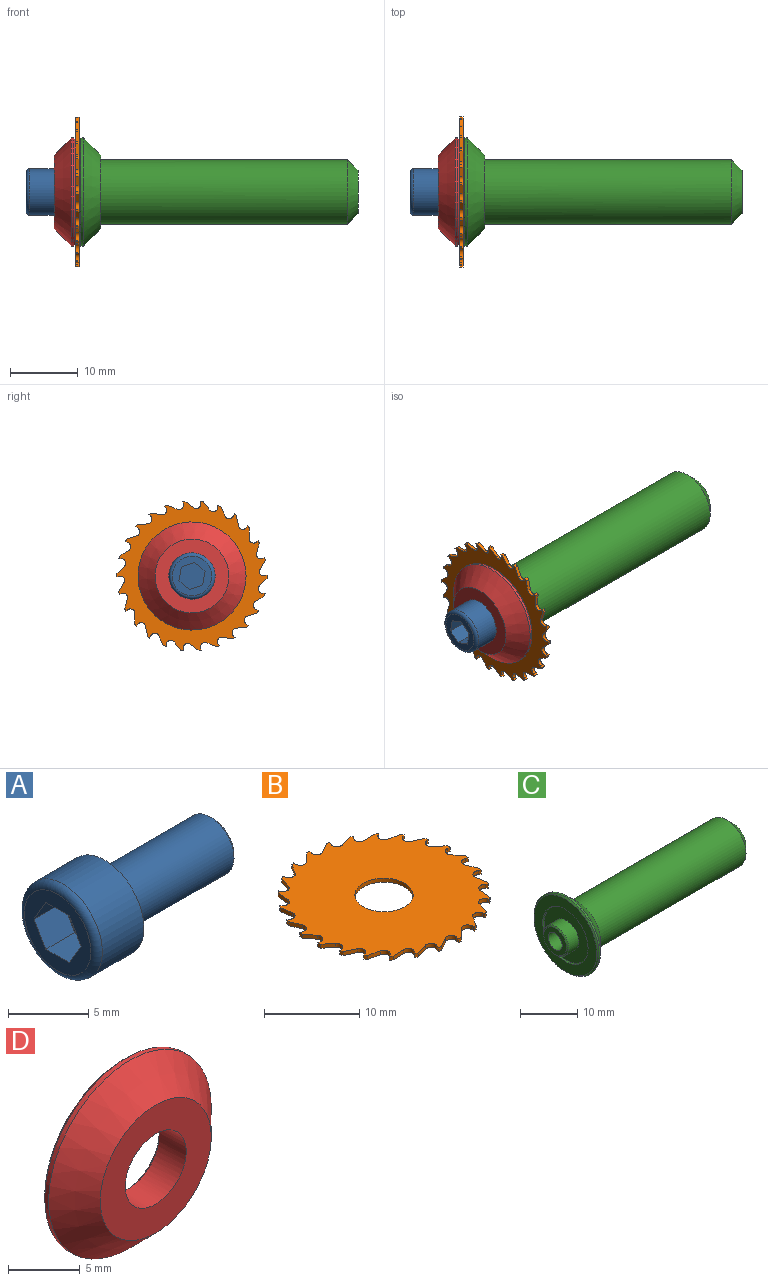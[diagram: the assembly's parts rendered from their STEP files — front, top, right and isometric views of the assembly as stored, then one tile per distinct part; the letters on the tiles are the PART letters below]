
ASSEMBLY  parts=4 mates=6
PART A: 14 faces, bbox 13.7x7.4x7.4 mm
  f0: plane 6.86x6.86mm, normal (1,0,0), area 23.3mm2, adj f1,f5
  f1: cylinder r=3.43mm len=6.86mm, axis (1,0,0), area 78.8mm2, adj f0,f2
  f2: torus R=2.92mm, axis (1,0,0), area 16.3mm2, adj f1,f3
  f3: plane 5.84x5.84mm, normal (-1,0,0), area 15.8mm2, adj f2,f6,f7,f8,f9,f10,f11
  f4: plane 3.66x3.66mm, normal (1,0,0), area 10.5mm2, adj f13
  f5: cylinder r=2.08mm len=9.27mm, axis (1,0,0), area 121.3mm2, adj f0,f13
  f6: plane 2.54x2.06mm, normal (0,0,1), area 5.2mm2, adj f3,f7,f11,f12
  f7: plane 2.54x1.79mm, normal (0,0.87,0.5), area 5.2mm2, adj f3,f6,f8,f12
  f8: plane 2.54x1.79mm, normal (0,0.87,-0.5), area 5.2mm2, adj f3,f7,f9,f12
  f9: plane 2.54x2.06mm, normal (0,0,-1), area 5.2mm2, adj f3,f8,f10,f12
  f10: plane 2.54x1.79mm, normal (0,-0.87,-0.5), area 5.2mm2, adj f3,f9,f11,f12
  f11: plane 2.54x1.79mm, normal (0,-0.87,0.5), area 5.2mm2, adj f3,f6,f10,f12
  f12: plane 4.12x3.57mm, normal (-1,0,0), area 11mm2, adj f6,f7,f8,f9,f10,f11
  f13: cone r=1.83mm half-angle=45deg, axis (-1,0,0), area 4.4mm2, adj f4,f5
PART B: 107 faces, bbox 22.1x22.2x0.5 mm
  f0: cylinder r=11.11mm len=0.51mm, axis (0,0,-1), area 0.2mm2, adj f9,f55,f70,f85
  f1: plane 0.51x0.27mm, normal (0.88,-0.48,0), area 0.2mm2, adj f8,f55,f85,f92
  f2: plane 1.45x0.62mm, normal (-0.92,-0.39,0), area 0.8mm2, adj f47,f55,f85,f106
  f3: cylinder r=11.11mm len=0.51mm, axis (0,0,-1), area 0.2mm2, adj f4,f41,f55,f85
  f4: plane 0.51x0.27mm, normal (-0.89,-0.45,0), area 0.2mm2, adj f3,f55,f85,f87
  f5: cylinder r=0.67mm len=1.23mm, axis (0,0,-1), area 0.8mm2, adj f55,f73,f77,f85
  f6: plane 0.51x0.3mm, normal (-1,0.02,0), area 0.2mm2, adj f55,f67,f85,f86
  f7: cylinder r=0.67mm len=1.12mm, axis (0,0,-1), area 0.8mm2, adj f55,f61,f85,f102
  f8: cylinder r=0.67mm len=0.99mm, axis (0,0,-1), area 0.8mm2, adj f1,f54,f55,f85
  f9: plane 1.22x1mm, normal (-0.63,-0.77,0), area 0.8mm2, adj f0,f10,f55,f85
  f10: cylinder r=0.67mm len=1.18mm, axis (0,0,-1), area 0.8mm2, adj f9,f55,f85,f95
  f11: plane 1.57x0.51mm, normal (-0.04,1,0), area 0.8mm2, adj f29,f55,f76,f85
  f12: cylinder r=11.11mm len=0.51mm, axis (0,0,-1), area 0.2mm2, adj f26,f50,f55,f85
  f13: cylinder r=11.11mm len=0.51mm, axis (0,0,-1), area 0.2mm2, adj f14,f55,f85,f102
  f14: plane 0.51x0.25mm, normal (-0.55,0.83,0), area 0.2mm2, adj f13,f22,f55,f85
  f15: cylinder r=0.67mm len=1.07mm, axis (0,0,-1), area 0.8mm2, adj f55,f85,f89,f98
  f16: plane 0.51x0.28mm, normal (0.37,0.93,0), area 0.2mm2, adj f55,f85,f91,f106
  f17: cylinder r=0.67mm len=1.21mm, axis (0,0,-1), area 0.8mm2, adj f28,f32,f55,f85
  f18: plane 1.49x0.51mm, normal (0.95,-0.32,0), area 0.8mm2, adj f48,f55,f85,f87
  f19: cylinder r=0.67mm len=1mm, axis (0,0,-1), area 0.8mm2, adj f27,f45,f55,f85
  f20: cylinder r=0.67mm len=1.06mm, axis (0,0,-1), area 0.8mm2, adj f55,f79,f85,f100
  f21: cylinder r=0.67mm len=0.93mm, axis (0,0,-1), area 0.8mm2, adj f55,f71,f74,f85
  f22: cylinder r=0.67mm len=1.21mm, axis (0,0,-1), area 0.8mm2, adj f14,f50,f55,f85
  f23: cylinder r=11.11mm len=0.51mm, axis (0,0,-1), area 0.2mm2, adj f55,f77,f83,f85
  f24: plane 0.51x0.27mm, normal (-0.88,0.48,0), area 0.2mm2, adj f30,f55,f65,f85
  f25: plane 1.42x0.68mm, normal (0.43,0.9,0), area 0.8mm2, adj f53,f55,f81,f85
  f26: plane 0.51x0.29mm, normal (-0.34,0.94,0), area 0.2mm2, adj f12,f55,f72,f85
  f27: plane 0.51x0.29mm, normal (-0.97,0.26,0), area 0.2mm2, adj f19,f36,f55,f85
  f28: plane 1.33x0.84mm, normal (-0.85,0.53,0), area 0.8mm2, adj f17,f37,f55,f85
  f29: cylinder r=11.11mm len=0.51mm, axis (0,0,-1), area 0.2mm2, adj f11,f55,f75,f85
  f30: cylinder r=11.11mm len=0.51mm, axis (0,0,-1), area 0.2mm2, adj f24,f45,f55,f85
  f31: plane 0.51x0.29mm, normal (0.97,-0.26,0), area 0.2mm2, adj f55,f85,f90,f96
  f32: plane 0.51x0.3mm, normal (0.98,0.22,0), area 0.2mm2, adj f17,f34,f55,f85
  f33: plane 0.51x0.3mm, normal (0.1,-0.99,0), area 0.2mm2, adj f46,f53,f55,f85
  f34: cylinder r=11.11mm len=0.51mm, axis (0,0,-1), area 0.2mm2, adj f32,f55,f73,f85
  f35: plane 1.26x0.95mm, normal (-0.8,-0.6,0), area 0.8mm2, adj f55,f62,f85,f91
  f36: cylinder r=11.11mm len=0.51mm, axis (0,0,-1), area 0.2mm2, adj f27,f52,f55,f85
  f37: cylinder r=11.11mm len=0.51mm, axis (0,0,-1), area 0.2mm2, adj f28,f55,f56,f85
  f38: plane 1.36x0.79mm, normal (-0.5,0.87,0), area 0.8mm2, adj f55,f85,f90,f92
  f39: cylinder r=11.11mm len=0.51mm, axis (0,0,-1), area 0.2mm2, adj f55,f61,f64,f85
  f40: plane 0.51x0.23mm, normal (-0.76,-0.65,0), area 0.2mm2, adj f55,f63,f85,f88
  f41: plane 1.57x0.51mm, normal (1,-0.08,0), area 0.8mm2, adj f3,f55,f85,f88
  f42: cylinder r=11.11mm len=0.51mm, axis (0,0,-1), area 0.2mm2, adj f54,f55,f58,f85
  f43: cylinder r=0.67mm len=1.13mm, axis (0,0,-1), area 0.8mm2, adj f49,f55,f56,f85
  f44: plane 1.42x0.68mm, normal (-0.43,-0.9,0), area 0.8mm2, adj f55,f72,f85,f103
  f45: plane 1.36x0.79mm, normal (0.5,-0.87,0), area 0.8mm2, adj f19,f30,f55,f85
  f46: cylinder r=0.67mm len=1.18mm, axis (0,0,-1), area 0.8mm2, adj f33,f55,f78,f85
  f47: cylinder r=11.11mm len=0.51mm, axis (0,0,-1), area 0.2mm2, adj f2,f55,f68,f85
  f48: cylinder r=11.11mm len=0.51mm, axis (0,0,-1), area 0.2mm2, adj f18,f55,f59,f85
  f49: plane 1.14x1.09mm, normal (-0.69,0.72,0), area 0.8mm2, adj f43,f55,f85,f96
  f50: plane 1.54x0.51mm, normal (-0.2,-0.98,0), area 0.8mm2, adj f12,f22,f55,f85
  f51: cylinder r=11.11mm len=0.51mm, axis (0,0,-1), area 0.2mm2, adj f55,f71,f79,f85
  f52: plane 1.14x1.09mm, normal (0.69,-0.72,0), area 0.8mm2, adj f36,f55,f85,f86
  f53: cylinder r=11.11mm len=0.51mm, axis (0,0,-1), area 0.2mm2, adj f25,f33,f55,f85
  f54: plane 1.51x0.51mm, normal (-0.28,0.96,0), area 0.8mm2, adj f8,f42,f55,f85
  f55: plane 22.21x22.12mm, normal (0,0,1), area 314.4mm2, adj f0,f1,f2,f3,f4,f5,f6,f7
  f56: plane 0.51x0.3mm, normal (1,-0.02,0), area 0.2mm2, adj f37,f43,f55,f85
  f57: cylinder r=0.67mm len=1.21mm, axis (0,0,-1), area 0.8mm2, adj f55,f59,f85,f104
  f58: plane 0.51x0.22mm, normal (0.74,-0.68,0), area 0.2mm2, adj f42,f55,f76,f85
  f59: plane 0.51x0.3mm, normal (-0.98,-0.22,0), area 0.2mm2, adj f48,f55,f57,f85
  f60: cylinder r=0.67mm len=1.17mm, axis (0,0,-1), area 0.8mm2, adj f55,f83,f85,f99
  f61: plane 0.51x0.22mm, normal (-0.74,0.68,0), area 0.2mm2, adj f7,f39,f55,f85
  f62: cylinder r=0.67mm len=1.07mm, axis (0,0,-1), area 0.8mm2, adj f35,f55,f70,f85
  f63: cylinder r=11.11mm len=0.51mm, axis (0,0,-1), area 0.2mm2, adj f40,f55,f85,f100
  f64: plane 1.51x0.51mm, normal (0.28,-0.96,0), area 0.8mm2, adj f39,f55,f65,f85
  f65: cylinder r=0.67mm len=0.99mm, axis (0,0,-1), area 0.8mm2, adj f24,f55,f64,f85
  f66: cylinder r=11.11mm len=0.51mm, axis (0,0,-1), area 0.2mm2, adj f55,f78,f85,f98
  f67: cylinder r=11.11mm len=0.51mm, axis (0,0,-1), area 0.2mm2, adj f6,f55,f85,f104
  f68: plane 0.51x0.25mm, normal (0.58,0.81,0), area 0.2mm2, adj f47,f55,f82,f85
  f69: cylinder r=0.67mm len=1.21mm, axis (0,0,-1), area 0.8mm2, adj f55,f75,f85,f101
  f70: plane 0.51x0.3mm, normal (0.14,0.99,0), area 0.2mm2, adj f0,f55,f62,f85
  f71: plane 1.45x0.62mm, normal (0.92,0.39,0), area 0.8mm2, adj f21,f51,f55,f85
  f72: cylinder r=0.67mm len=1.23mm, axis (0,0,-1), area 0.8mm2, adj f26,f44,f55,f85
  f73: plane 1.49x0.51mm, normal (-0.95,0.32,0), area 0.8mm2, adj f5,f34,f55,f85
  f74: plane 0.51x0.28mm, normal (-0.37,-0.93,0), area 0.2mm2, adj f21,f55,f85,f97
  f75: plane 0.51x0.25mm, normal (0.55,-0.83,0), area 0.2mm2, adj f29,f55,f69,f85
  f76: cylinder r=0.67mm len=1.12mm, axis (0,0,-1), area 0.8mm2, adj f11,f55,f58,f85
  f77: plane 0.51x0.27mm, normal (0.89,0.45,0), area 0.2mm2, adj f5,f23,f55,f85
  f78: plane 1.22x1mm, normal (0.63,0.77,0), area 0.8mm2, adj f46,f55,f66,f85
  f79: plane 0.51x0.25mm, normal (-0.58,-0.81,0), area 0.2mm2, adj f20,f51,f55,f85
  f80: plane 1.56x0.51mm, normal (-0.99,-0.16,0), area 0.8mm2, adj f55,f82,f85,f94
  f81: cylinder r=0.67mm len=1.23mm, axis (0,0,-1), area 0.8mm2, adj f25,f55,f85,f93
  f82: cylinder r=0.67mm len=1.06mm, axis (0,0,-1), area 0.8mm2, adj f55,f68,f80,f85
  f83: plane 1.57x0.51mm, normal (-1,0.08,0), area 0.8mm2, adj f23,f55,f60,f85
  f84: cylinder r=3.05mm len=6.1mm, axis (0,0,-1), area 9.7mm2, adj f55,f85
  f85: plane 22.21x22.12mm, normal (0,0,-1), area 314.4mm2, adj f0,f1,f2,f3,f4,f5,f6,f7
  f86: cylinder r=0.67mm len=1.13mm, axis (0,0,-1), area 0.8mm2, adj f6,f52,f55,f85
  f87: cylinder r=0.67mm len=1.23mm, axis (0,0,-1), area 0.8mm2, adj f4,f18,f55,f85
  f88: cylinder r=0.67mm len=1.17mm, axis (0,0,-1), area 0.8mm2, adj f40,f41,f55,f85
  f89: plane 1.26x0.95mm, normal (0.8,0.6,0), area 0.8mm2, adj f15,f55,f85,f97
  f90: cylinder r=0.67mm len=1mm, axis (0,0,-1), area 0.8mm2, adj f31,f38,f55,f85
  f91: cylinder r=11.11mm len=0.51mm, axis (0,0,-1), area 0.2mm2, adj f16,f35,f55,f85
  f92: cylinder r=11.11mm len=0.51mm, axis (0,0,-1), area 0.2mm2, adj f1,f38,f55,f85
  f93: plane 0.51x0.29mm, normal (0.34,-0.94,0), area 0.2mm2, adj f55,f81,f85,f105
  f94: cylinder r=11.11mm len=0.51mm, axis (0,0,-1), area 0.2mm2, adj f55,f80,f85,f99
  f95: plane 0.51x0.3mm, normal (-0.1,0.99,0), area 0.2mm2, adj f10,f55,f85,f103
  f96: cylinder r=11.11mm len=0.51mm, axis (0,0,-1), area 0.2mm2, adj f31,f49,f55,f85
  f97: cylinder r=11.11mm len=0.51mm, axis (0,0,-1), area 0.2mm2, adj f55,f74,f85,f89
  f98: plane 0.51x0.3mm, normal (-0.14,-0.99,0), area 0.2mm2, adj f15,f55,f66,f85
  f99: plane 0.51x0.23mm, normal (0.76,0.65,0), area 0.2mm2, adj f55,f60,f85,f94
  f100: plane 1.56x0.51mm, normal (0.99,0.16,0), area 0.8mm2, adj f20,f55,f63,f85
  f101: plane 1.54x0.51mm, normal (0.2,0.98,0), area 0.8mm2, adj f55,f69,f85,f105
  f102: plane 1.57x0.51mm, normal (0.04,-1,0), area 0.8mm2, adj f7,f13,f55,f85
  f103: cylinder r=11.11mm len=0.51mm, axis (0,0,-1), area 0.2mm2, adj f44,f55,f85,f95
  f104: plane 1.33x0.84mm, normal (0.85,-0.53,0), area 0.8mm2, adj f55,f57,f67,f85
  f105: cylinder r=11.11mm len=0.51mm, axis (0,0,-1), area 0.2mm2, adj f55,f85,f93,f101
  f106: cylinder r=0.67mm len=0.93mm, axis (0,0,-1), area 0.8mm2, adj f2,f16,f55,f85
PART C: 18 faces, bbox 43.8x16x16 mm
  f0: plane 10.92x10.92mm, normal (1,0,0), area 22.4mm2, adj f8,f17
  f1: cylinder r=8mm len=16mm, axis (1,0,0), area 19.2mm2, adj f15,f17
  f2: plane 15.49x15.49mm, normal (-1,0,0), area 90.4mm2, adj f3,f15
  f3: cone r=5.59mm half-angle=30deg, axis (-1,0,0), area 10.2mm2, adj f2,f4
  f4: plane 10.88x10.88mm, normal (-1,0,0), area 63.8mm2, adj f3,f5
  f5: cylinder r=3.05mm len=6.1mm, axis (1,0,0), area 48.6mm2, adj f4,f16
  f6: plane 5.59x5.59mm, normal (-1,0,0), area 15.2mm2, adj f10,f16
  f7: plane 6.48x6.48mm, normal (1,0,0), area 25mm2, adj f11,f14
  f8: cylinder r=4.76mm len=36.58mm, axis (1,0,0), area 1094.5mm2, adj f0,f14
  f9: cone r=0mm half-angle=59deg, axis (-1,0,0), area 10.9mm2, adj f10
  f10: cylinder r=1.73mm len=15.72mm, axis (-1,0,0), area 170.6mm2, adj f6,f9
  f11: cone r=1.59mm half-angle=30deg, axis (1,0,0), area 13.6mm2, adj f7,f12
  f12: cylinder r=0.6mm len=1.19mm, axis (1,0,0), area 4.5mm2, adj f11,f13
  f13: cone r=0.6mm half-angle=60deg, axis (1,0,0), area 1.3mm2, adj f12
  f14: cone r=3.24mm half-angle=45deg, axis (-1,0,0), area 54.2mm2, adj f7,f8
  f15: cone r=8mm half-angle=45deg, axis (1,0,0), area 17.8mm2, adj f1,f2
  f16: cone r=3.05mm half-angle=45deg, axis (1,0,0), area 6.6mm2, adj f5,f6
  f17: cone r=5.46mm half-angle=45deg, axis (-1,0,0), area 151.9mm2, adj f0,f1
PART D: 9 faces, bbox 16x3.2x16 mm
  f0: cylinder r=3mm len=6mm, axis (0,1,0), area 50.3mm2, adj f2,f7
  f1: cylinder r=8mm len=16mm, axis (0,1,0), area 19.2mm2, adj f6,f8
  f2: plane 10.92x10.92mm, normal (0,-1,0), area 65.4mm2, adj f0,f8
  f3: plane 15.49x15.49mm, normal (0,1,0), area 90.4mm2, adj f5,f6
  f4: plane 10.88x10.88mm, normal (0,1,0), area 59.8mm2, adj f5,f7
  f5: cone r=5.44mm half-angle=30deg, axis (0,1,0), area 10.2mm2, adj f3,f4
  f6: cone r=8mm half-angle=45deg, axis (0,-1,0), area 17.8mm2, adj f1,f3
  f7: cone r=3mm half-angle=45deg, axis (0,1,0), area 7.1mm2, adj f0,f4
  f8: cone r=5.46mm half-angle=45deg, axis (0,1,0), area 151.9mm2, adj f1,f2
PLACE A rot(axis=(-1,0,0),79.9deg) t=(-5.31,0,0)mm
PLACE B rot(axis=(0,1,0),90deg) t=(2.54,0,0)mm
PLACE C at identity fixed
PLACE D rot(axis=(0.61,0.61,-0.51),126deg) t=(2.03,0,0)mm
MATE cylindrical A.f1 <-> C.f1  axis (1,0,0) through (-1.14,0,0)mm
MATE planar C.f1 <-> B.f53  axis (-1,0,0) through (2.54,0,0)mm
MATE cylindrical D.f0 <-> C.f1  axis (1,0,0) through (1.52,0,0)mm
MATE planar D.f1 <-> A.f1  axis (-1,0,0) through (-1.14,0,0)mm
MATE planar D.f1 <-> B.f12  axis (1,0,0) through (2.03,0,0)mm
MATE cylindrical B.f53 <-> C.f1  axis (1,0,0) through (2.54,0,0)mm
